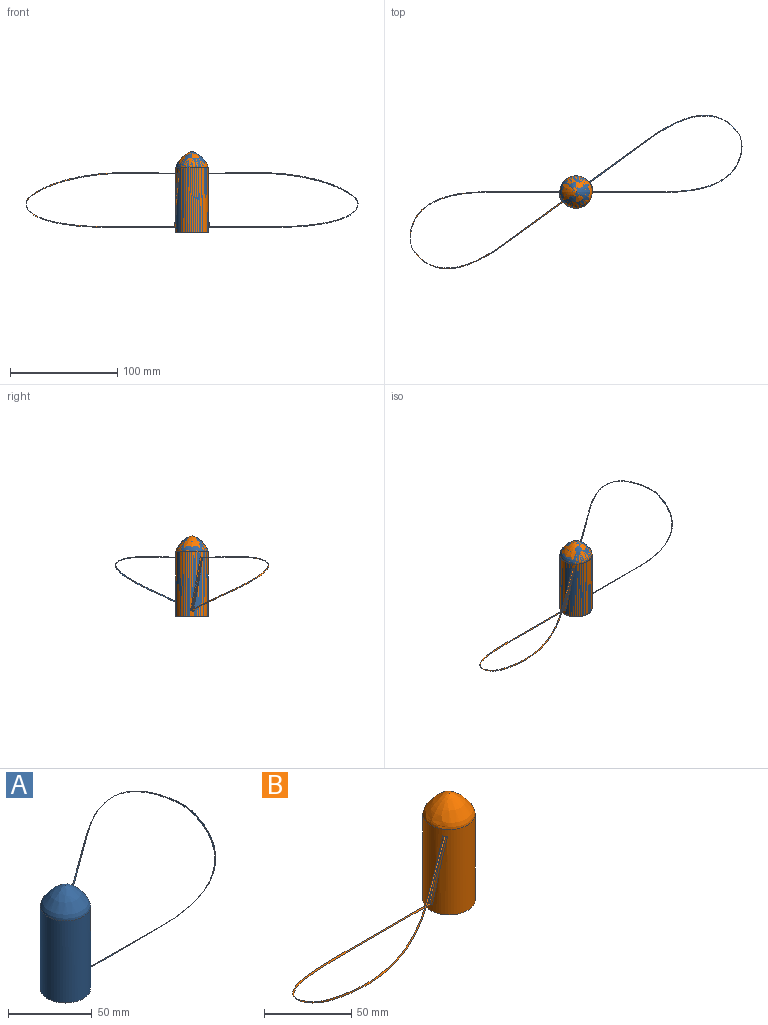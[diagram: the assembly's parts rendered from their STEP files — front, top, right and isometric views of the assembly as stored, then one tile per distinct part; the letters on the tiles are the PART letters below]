
ASSEMBLY  parts=2 mates=1
PART A: 10 faces, bbox 192.9x108.6x131.5 mm
  f0: cylinder r=15mm len=60mm, axis (0,0,-1), area 5511.3mm2, adj f1,f2,f3,f4,f5,f6
  f1: bspline ~89x2.81mm, area 67.5mm2, adj f0,f5,f6,f7
  f2: bspline ~73.34x54.16mm, area 67.6mm2, adj f0,f5,f6,f8
  f3: plane 30x30mm, normal (0,0,-1), area 706.9mm2, adj f0
  f4: bspline ~29.99x29.97mm, area 1236.4mm2, adj f0
  f5: bspline ~60.39x11.04mm, area 75.4mm2, adj f0,f1,f2
  f6: bspline ~60.39x12.09mm, area 75.4mm2, adj f0,f1,f2
  f7: bspline ~100.93x100.45mm, area 99.7mm2, adj f1,f9
  f8: bspline ~101.57x94.77mm, area 99.9mm2, adj f2,f9
  f9: bspline ~18.68x16.6mm, area 15mm2, adj f7,f8
PART B: 10 faces, bbox 192.9x108.6x131.5 mm
  f0: cylinder r=15mm len=60mm, axis (0,0,-1), area 5511.3mm2, adj f1,f2,f3,f4,f5,f6
  f1: bspline ~89x2.81mm, area 67.5mm2, adj f0,f5,f6,f7
  f2: bspline ~73.34x54.16mm, area 67.6mm2, adj f0,f5,f6,f8
  f3: plane 30x30mm, normal (0,0,-1), area 706.9mm2, adj f0
  f4: bspline ~29.99x29.97mm, area 1236.4mm2, adj f0
  f5: bspline ~60.39x11.04mm, area 75.4mm2, adj f0,f1,f2
  f6: bspline ~60.39x12.09mm, area 75.4mm2, adj f0,f1,f2
  f7: bspline ~100.93x100.45mm, area 99.7mm2, adj f1,f9
  f8: bspline ~101.57x94.77mm, area 99.9mm2, adj f2,f9
  f9: bspline ~18.68x16.6mm, area 15mm2, adj f7,f8
PLACE A t=(0,0,5)mm
PLACE B t=(0,0,5)mm
MATE fastened A.f0 <-> B.f0  axis (0,0,-1) through (0,0,0)mm
